# Revit family: F300
name_source: partatom
category: Modelos genéricos
revit_build: Autodesk Revit 2017 (Build: 20170118_1100(x64)
units: mm (PartAtom-declared; Revit-internal decimal feet)

## family parameters
Compartido = No
Corte con vacíos al cargar = No
Cota de conector redondo = Diámetro de uso
Puede alojar armadura = No
Punto de cálculo de habitación = No
Tipo de pieza = Normal

## types (1)
- F300K00R
    Altura = 362 mm  [stored 1.18766 ft]
    Anchura exterior = 362 mm  [stored 1.18766 ft]
    Anchura interior = 300 mm  [stored 0.984252 ft]
    Caudal de referencia = 0 L/s
    Clase de carga = F-900 Norma EN-1433
    Costo = 83.78€
    Descripción = Canal de Hormigón Polímero tipo ULMA / modelo F100K / ancho exterior 156mm / ancho interior 100mm y con alturas exteriores disponibles entre 190mm y 310 mm / con posibilidad de instalación en pendiente tipo cascada / para recogida de aguas pluviales / en módulos de 1 ML de longitud / fijación de seguridad en 8 puntos por ML / perfiles de acero galvanizado* para protección lateral.
    Fabricante = ULMA Architectural
    Ficha técnica = http://www.ulmaarchitectural.com
    Modelo = F300
    Pendiente = 0.00%
    Peso = 0.00 kg
    Sección hidráulica = 126.00 cm²
    URL = http://www.ulmaarchitectural.com
    Ø salida horizontal = 110 mm
    Ø salida vertical = 110 mm

note: [stored X ft] marks values corroborated as IEEE doubles in the binary element streams (Revit-internal decimal feet)
